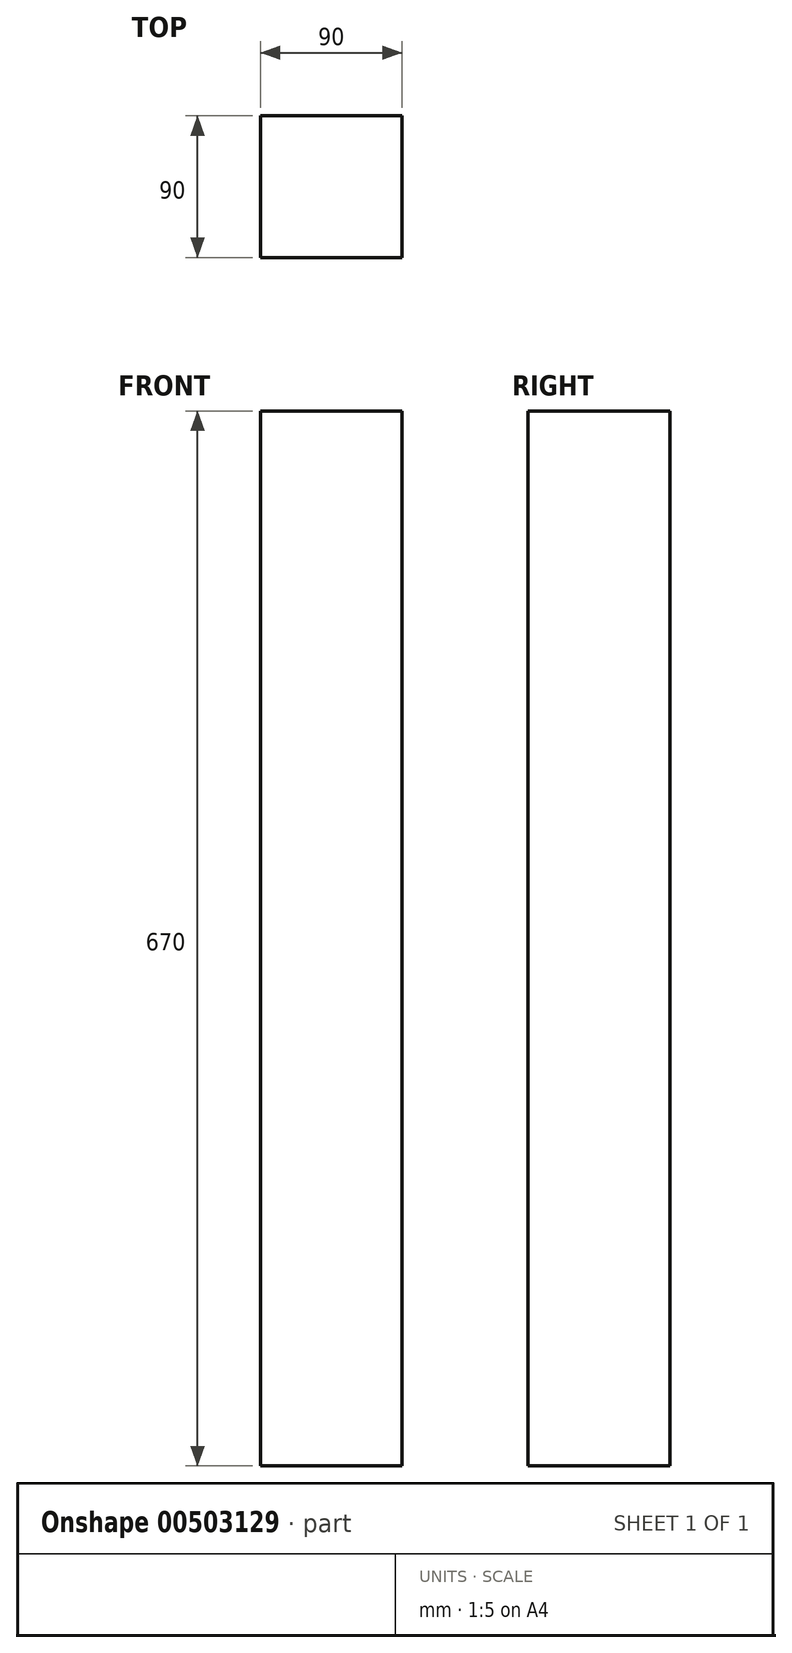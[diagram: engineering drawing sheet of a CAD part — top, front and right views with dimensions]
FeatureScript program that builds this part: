
annotation { "Feature Type Name" : "Feature", "Feature Type Description" : "" }
export const myFeature = defineFeature(function(context is Context, id is Id, definition is map)
    precondition{}
    {
        {
            var Q0;
            Q0=qCreatedBy(makeId("Top.planeOp"),FACE);
            var sketch = newSketch(context, id + "F0", { "sketchPlane" : qUnion([Q0])});
            skLineSegment(sketch, "E0.bottom", {"start": v(-45, 45) * mm, "end": v(45, 45) * mm});
            skLineSegment(sketch, "E0.top", {"start": v(-45, -45) * mm, "end": v(45, -45) * mm});
            skLineSegment(sketch, "E0.left", {"start": v(-45, 45) * mm, "end": v(-45, -45) * mm});
            skLineSegment(sketch, "E0.right", {"start": v(45, 45) * mm, "end": v(45, -45) * mm});
            skSolve(sketch);
        }
        {
            var Q0;
            Q0=makeQuery(id+"F0.imprint","IMPRINT",FACE,{"disambiguationData":[TD([[makeQuery(id+"F0.imprint","IMPRINT",EDGE,{"derivedFrom":sQuery(id+"F0.wireOp",EDGE,"E0.bottom")}),-1.0]])]});
            extrude(context, id + "F1", {"entities" : qUnion([Q0]), "depth" : (800 - 30 - 100) * mm, "offsetDistance" : 25 * mm});
        }
        {
            var Q0;
            Q0=makeQuery(id+"F1.opExtrude","SWEPT_FACE",FACE,{"disambiguationData":[OSD([sQuery(id+"F0.wireOp",EDGE,"E0.top")])]});
            var sketch = newSketch(context, id + "F2", { "sketchPlane" : qUnion([Q0])});
            skLineSegment(sketch, "E1", {"start": v(-45, 100) * mm, "end": v(45, 100) * mm, "construction": true});
            skSolve(sketch);
        }
    });
